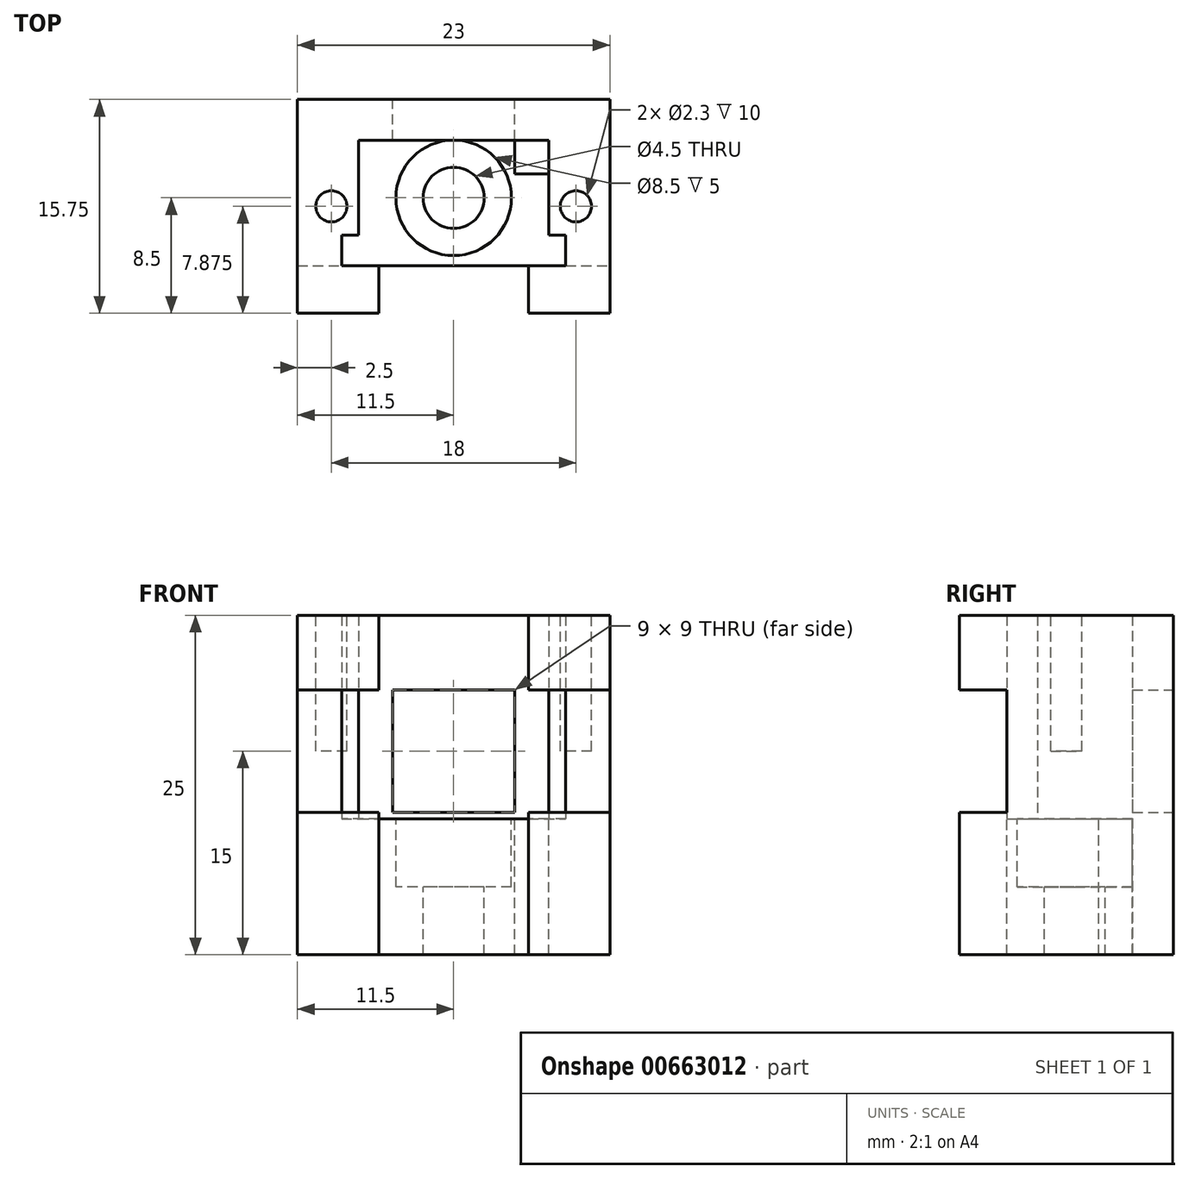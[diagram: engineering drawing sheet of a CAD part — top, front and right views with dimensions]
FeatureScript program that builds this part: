
annotation { "Feature Type Name" : "Feature", "Feature Type Description" : "" }
export const myFeature = defineFeature(function(context is Context, id is Id, definition is map)
    precondition{}
    {
        {
            var Q0;
            Q0=qCreatedBy(makeId("Top.planeOp"),FACE);
            var sketch = newSketch(context, id + "F0", { "sketchPlane" : qUnion([Q0])});
            skLineSegment(sketch, "E0.bottom", {"start": v(11.5, -10) * mm, "end": v(-11.5, -10) * mm});
            skLineSegment(sketch, "E0.top", {"start": v(11.5, 10) * mm, "end": v(-11.5, 10) * mm});
            skLineSegment(sketch, "E0.left", {"start": v(11.5, -10) * mm, "end": v(11.5, 10) * mm});
            skLineSegment(sketch, "E0.right", {"start": v(-11.5, -10) * mm, "end": v(-11.5, 10) * mm});
            skPoint(sketch, "E0.middle", {"position": v(0, 0) * mm});
            skSolve(sketch);
        }
        {
            var Q0;
            Q0=makeQuery(id+"F0.imprint","IMPRINT",FACE,{"disambiguationData":[TD([[makeQuery(id+"F0.imprint","IMPRINT",EDGE,{"derivedFrom":sQuery(id+"F0.wireOp",EDGE,"E0.bottom")}),-1.0]])]});
            extrude(context, id + "F1", {"entities" : qUnion([Q0]), "depth" : 10 * mm, "offsetDistance" : 25 * mm});
        }
        {
            var Q0;
            Q0=makeQuery(id+"F1.opExtrude","CAP_FACE",FACE,{"disambiguationData":[OSD([sQuery(id+"F0.wireOp",EDGE,"E0.bottom"),sQuery(id+"F0.wireOp",EDGE,"E0.top"),sQuery(id+"F0.wireOp",EDGE,"E0.left"),sQuery(id+"F0.wireOp",EDGE,"E0.right")])],"isStart":false});
            var sketch = newSketch(context, id + "F2", { "sketchPlane" : qUnion([Q0])});
            skLineSegment(sketch, "E1", {"start": v(-5.5, -10) * mm, "end": v(-5.5, -6.5) * mm});
            skLineSegment(sketch, "E2", {"start": v(-5.5, -6.5) * mm, "end": v(-8.25, -6.5) * mm});
            skLineSegment(sketch, "E3", {"start": v(-8.25, -6.5) * mm, "end": v(-8.25, -4.25) * mm});
            skLineSegment(sketch, "E4", {"start": v(-11.5, -0.75) * mm, "end": v(-11.5, -10) * mm});
            skLineSegment(sketch, "E5", {"start": v(-11.5, -10) * mm, "end": v(-5.5, -10) * mm});
            skLineSegment(sketch, "E6", {"start": v(5.5, -10) * mm, "end": v(5.5, -6.5) * mm});
            skLineSegment(sketch, "E7", {"start": v(5.5, -6.5) * mm, "end": v(8.25, -6.5) * mm});
            skLineSegment(sketch, "E8", {"start": v(8.25, -6.5) * mm, "end": v(8.25, -4.25) * mm});
            skLineSegment(sketch, "E9", {"start": v(11.5, -10) * mm, "end": v(5.5, -10) * mm});
            skLineSegment(sketch, "E10", {"start": v(-8.25, -4.25) * mm, "end": v(-7, -4.25) * mm});
            skLineSegment(sketch, "E11", {"start": v(-7, -4.25) * mm, "end": v(-7, -0.75) * mm});
            skLineSegment(sketch, "E12", {"start": v(-7, -0.75) * mm, "end": v(-11.5, -0.75) * mm});
            skLineSegment(sketch, "E13", {"start": v(8.25, -4.25) * mm, "end": v(7, -4.25) * mm});
            skLineSegment(sketch, "E14", {"start": v(7, -4.25) * mm, "end": v(7, -0.75) * mm});
            skLineSegment(sketch, "E15", {"start": v(7, -0.75) * mm, "end": v(11.5, -0.75) * mm});
            skLineSegment(sketch, "E16", {"start": v(11.5, -0.75) * mm, "end": v(11.5, -10) * mm});
            skSolve(sketch);
        }
        {
            var Q0;
            Q0=makeQuery(id+"F2.imprint","IMPRINT",FACE,{"disambiguationData":[TD([[makeQuery(id+"F2.imprint","IMPRINT",EDGE,{"derivedFrom":sQuery(id+"F2.wireOp",EDGE,"E6")}),-1.0]])]});
            var Q1;
            Q1=makeQuery(id+"F2.imprint","IMPRINT",FACE,{"disambiguationData":[TD([[makeQuery(id+"F2.imprint","IMPRINT",EDGE,{"derivedFrom":sQuery(id+"F2.wireOp",EDGE,"E1")}),1.0]])]});
            extrude(context, id + "F3", {"entities" : qUnion([Q0, Q1]), "operationType" : NewBodyOperationType.ADD, "depth" : 15 * mm, "offsetDistance" : 25 * mm});
        }
        {
            var Q0;
            Q0=makeQuery(id+"F1.opExtrude","CAP_FACE",FACE,{"disambiguationData":[OSD([sQuery(id+"F0.wireOp",EDGE,"E0.bottom"),sQuery(id+"F0.wireOp",EDGE,"E0.top"),sQuery(id+"F0.wireOp",EDGE,"E0.left"),sQuery(id+"F0.wireOp",EDGE,"E0.right")])],"isStart":false});
            var sketch = newSketch(context, id + "F4", { "sketchPlane" : qUnion([Q0])});
            skLineSegment(sketch, "E17.bottom", {"start": v(-5.5, -6.5) * mm, "end": v(5.5, -6.5) * mm});
            skLineSegment(sketch, "E17.top", {"start": v(-5.5, -10) * mm, "end": v(5.5, -10) * mm});
            skLineSegment(sketch, "E17.left", {"start": v(-5.5, -6.5) * mm, "end": v(-5.5, -10) * mm});
            skLineSegment(sketch, "E17.right", {"start": v(5.5, -6.5) * mm, "end": v(5.5, -10) * mm});
            skSolve(sketch);
        }
        {
            var Q0;
            Q0=makeQuery(id+"F4.imprint","IMPRINT",FACE,{"disambiguationData":[TD([[makeQuery(id+"F4.imprint","IMPRINT",EDGE,{"derivedFrom":sQuery(id+"F4.wireOp",EDGE,"E17.bottom")}),-1.0]])]});
            extrude(context, id + "F5", {"entities" : qUnion([Q0]), "operationType" : NewBodyOperationType.REMOVE, "endBound" : BoundingType.THROUGH_ALL, "oppositeDirection" : true, "depth" : 25 * mm, "offsetDistance" : 25 * mm});
        }
        {
            var Q0;
            Q0=makeQuery(id+"F3.opExtrude","SWEPT_FACE",FACE,{"disambiguationData":[OSD([sQuery(id+"F2.wireOp",EDGE,"E15")])]});
            var Q1;
            Q1=makeQuery(id+"F3.opExtrude","SWEPT_FACE",FACE,{"disambiguationData":[OSD([sQuery(id+"F2.wireOp",EDGE,"E12")])]});
            extrude(context, id + "F6", {"entities" : qUnion([Q0, Q1]), "operationType" : NewBodyOperationType.ADD, "depth" : 3.5 * mm, "offsetDistance" : 25 * mm});
        }
        {
            var Q0;
            Q0=makeQuery(id+"F6.opExtrude","CAP_FACE",FACE,{"disambiguationData":[OSD([sQuery(id+"F2.wireOp",EDGE,"E15")])],"isStart":false});
            var sketch = newSketch(context, id + "F7", { "sketchPlane" : qUnion([Q0])});
            skLineSegment(sketch, "E18.bottom", {"start": v(-11.5, 25) * mm, "end": v(11.5, 25) * mm});
            skLineSegment(sketch, "E18.top", {"start": v(-11.5, 10) * mm, "end": v(11.5, 10) * mm});
            skLineSegment(sketch, "E18.left", {"start": v(-11.5, 25) * mm, "end": v(-11.5, 10) * mm});
            skLineSegment(sketch, "E18.right", {"start": v(11.5, 25) * mm, "end": v(11.5, 10) * mm});
            skSolve(sketch);
        }
        {
            var Q0;
            {var subQ14=sQuery(id+"F7.wireOp",EDGE,"E18.left");Q0=makeQuery(id+"F7.imprint","IMPRINT",FACE,{"disambiguationData":[TD([[makeQuery(id+"F7.imprint","IMPRINT",EDGE,{"derivedFrom":subQ14}),1.0]])]});}
            var Q1;
            {var subQ0=sQuery(id+"F7.wireOp",EDGE,"E18.right");Q1=makeQuery(id+"F7.imprint","IMPRINT",FACE,{"disambiguationData":[TD([[makeQuery(id+"F7.imprint","IMPRINT",EDGE,{"derivedFrom":subQ0}),-1.0]])]});}
            var Q2;
            {var subQ1=sQuery(id+"F2.wireOp",EDGE,"E15");Q2=makeQuery(id+"F7.imprint","IMPRINT",FACE,{"disambiguationData":[TD([[makeQuery(id+"F7.imprint","IMPRINT",EDGE,{"derivedFrom":makeQuery(id+"F6.opExtrude","CAP_EDGE",EDGE,{"disambiguationData":[OSD([subQ1,sQuery(id+"FgVDrUZru3OC2iL_1.wireOp",EDGE,"WYO9HxfS-uRYI-8hlX-gOUZ-VxZhSrOw4LOQ.bottom")])],"isStart":false})}),-1.0]])]});}
            extrude(context, id + "F8", {"entities" : qUnion([Q0, Q1, Q2]), "operationType" : NewBodyOperationType.ADD, "depth" : 3 * mm, "offsetDistance" : 25 * mm});
        }
        {
            var Q0;
            Q0=makeQuery(id+"F1.opExtrude","SWEPT_FACE",FACE,{"disambiguationData":[OSD([sQuery(id+"F0.wireOp",EDGE,"E0.top")])]});
            extrude(context, id + "F9", {"entities" : qUnion([Q0]), "operationType" : NewBodyOperationType.ADD, "depth" : 7 * mm, "offsetDistance" : 25 * mm});
        }
        {
            var Q0;
            {var subQ0=sQuery(id+"F0.wireOp",EDGE,"E0.top");var subQ1=sQuery(id+"F0.wireOp",EDGE,"E0.right");var subQ4=sQuery(id+"F0.wireOp",EDGE,"E0.left");Q0=makeQuery(id+"F9.boolean.opBoolean","MERGE",FACE,{"derivedFrom":[makeQuery(id+"F8.boolean.opBoolean","SPLIT",FACE,{"disambiguationData":[TD([makeQuery(id+"F1.opExtrude","SWEPT_FACE",FACE,{"disambiguationData":[OSD([subQ0])]})])],"derivedFrom":makeQuery(id+"F00eLFHubhNlvBN_1.boolean.opBoolean","MERGE",FACE,{"derivedFrom":[makeQuery(id+"F1.opExtrude","CAP_FACE",FACE,{"disambiguationData":[OSD([sQuery(id+"F0.wireOp",EDGE,"E0.bottom"),subQ0,subQ4,subQ1])],"isStart":false})],"fromTools":[makeQuery(id+"F00eLFHubhNlvBN_1.opExtrude","SWEPT_FACE",FACE,{"disambiguationData":[OSD([sQuery(id+"FP4EQcqf4ovbBqS_1.wireOp",EDGE,"o0LPASs0-g3RE-xfQt-ammR-mRPTQmorZibc.bottom")])]})]})}),makeQuery(id+"F9.opExtrude","SWEPT_FACE",FACE,{"disambiguationData":[OSD([subQ0]),TDD([makeQuery(id+"F1.opExtrude","CAP_EDGE",EDGE,{"disambiguationData":[OSD([subQ0])],"isStart":false})])]})]});}
            var sketch = newSketch(context, id + "F10", { "sketchPlane" : qUnion([Q0])});
            skCircle(sketch, "E19", {"center": v(0, 11.25) * mm, "radius": 2.5 * mm});
            skCircle(sketch, "E20", {"center": v(0, 11.25) * mm, "radius": 5 * mm});
            skSolve(sketch);
        }
        {
            var Q0;
            Q0=makeQuery(id+"F10.imprint","IMPRINT",FACE,{"disambiguationData":[TD([[makeQuery(id+"F10.imprint","IMPRINT",EDGE,{"derivedFrom":sQuery(id+"F10.wireOp",EDGE,"E19")}),1.0]])]});
            extrude(context, id + "F11", {"entities" : qUnion([Q0]), "operationType" : NewBodyOperationType.REMOVE, "endBound" : BoundingType.THROUGH_ALL, "oppositeDirection" : true, "depth" : 25 * mm, "offsetDistance" : 25 * mm});
        }
        {
            var Q0;
            Q0=makeQuery(id+"F10.imprint","IMPRINT",FACE,{"disambiguationData":[TD([[makeQuery(id+"F10.imprint","IMPRINT",EDGE,{"derivedFrom":sQuery(id+"F10.wireOp",EDGE,"E19")}),-1.0]])]});
            extrude(context, id + "F12", {"entities" : qUnion([Q0]), "operationType" : NewBodyOperationType.REMOVE, "oppositeDirection" : true, "depth" : 4.5 * mm, "offsetDistance" : 25 * mm});
        }
        {
            var Q0;
            {var subQ0=sQuery(id+"F0.wireOp",EDGE,"E0.right");var subQ1=sQuery(id+"F2.wireOp",EDGE,"E4");Q0=makeQuery(id+"F9.boolean.opBoolean","MERGE",FACE,{"derivedFrom":[makeQuery(id+"F8.boolean.opBoolean","MERGE",FACE,{"derivedFrom":[makeQuery(id+"F6.boolean.opBoolean","MERGE",FACE,{"derivedFrom":[makeQuery(id+"F3.boolean.opBoolean","MERGE",FACE,{"derivedFrom":[makeQuery(id+"F1.opExtrude","SWEPT_FACE",FACE,{"disambiguationData":[OSD([subQ0])]}),makeQuery(id+"F3.opExtrude","SWEPT_FACE",FACE,{"disambiguationData":[OSD([subQ1])]})]}),makeQuery(id+"F6.opExtrude","SWEPT_FACE",FACE,{"disambiguationData":[OSD([subQ0,subQ1,sQuery(id+"F2.wireOp",EDGE,"E12")])]})]}),makeQuery(id+"F8.opExtrude","SWEPT_FACE",FACE,{"disambiguationData":[OSD([sQuery(id+"F7.wireOp",EDGE,"E18.right")])]})]}),makeQuery(id+"F9.opExtrude","SWEPT_FACE",FACE,{"disambiguationData":[OSD([sQuery(id+"F0.wireOp",EDGE,"E0.top"),subQ0])]})]});}
            var sketch = newSketch(context, id + "F13", { "sketchPlane" : qUnion([Q0])});
            skCircle(sketch, "E21", {"center": v(0, 5) * mm, "radius": 1.5 * mm});
            skSolve(sketch);
        }
        {
            var Q0;
            Q0=makeQuery(id+"F9.opExtrude","CAP_FACE",FACE,{"disambiguationData":[OSD([sQuery(id+"F0.wireOp",EDGE,"E0.top")])],"isStart":false});
            var sketch = newSketch(context, id + "F14", { "sketchPlane" : qUnion([Q0])});
            skCircle(sketch, "E22", {"center": v(8.5, 5) * mm, "radius": 1.5 * mm});
            skSolve(sketch);
        }
        {
            var Q0;
            Q0=makeQuery(id+"F8.boolean.opBoolean","SPLIT",FACE,{"disambiguationData":[TD([makeQuery(id+"F3.opExtrude","SWEPT_FACE",FACE,{"disambiguationData":[OSD([sQuery(id+"F2.wireOp",EDGE,"E1")])]})])],"derivedFrom":makeQuery(id+"F1.opExtrude","CAP_FACE",FACE,{"disambiguationData":[OSD([sQuery(id+"F0.wireOp",EDGE,"E0.bottom"),sQuery(id+"F0.wireOp",EDGE,"E0.top"),sQuery(id+"F0.wireOp",EDGE,"E0.left"),sQuery(id+"F0.wireOp",EDGE,"E0.right")])],"isStart":false})});
            var sketch = newSketch(context, id + "F15", { "sketchPlane" : qUnion([Q0])});
            skCircle(sketch, "E23", {"center": v(-4, 0) * mm, "radius": 1.5 * mm});
            skSolve(sketch);
        }
        {
            var Q0;
            {var subQ0=sQuery(id+"F2.wireOp",EDGE,"E15");var subQ1=sQuery(id+"F2.wireOp",EDGE,"E12");Q0=makeQuery(id+"F8.boolean.opBoolean","MERGE",FACE,{"derivedFrom":[makeQuery(id+"F6.boolean.opBoolean","MERGE",FACE,{"derivedFrom":[makeQuery(id+"F3.opExtrude","CAP_FACE",FACE,{"disambiguationData":[OSD([sQuery(id+"F2.wireOp",EDGE,"E1"),sQuery(id+"F2.wireOp",EDGE,"E2"),sQuery(id+"F2.wireOp",EDGE,"E3"),sQuery(id+"F2.wireOp",EDGE,"E4"),sQuery(id+"F2.wireOp",EDGE,"E5"),sQuery(id+"F2.wireOp",EDGE,"E10"),sQuery(id+"F2.wireOp",EDGE,"E11"),subQ1])],"isStart":false}),makeQuery(id+"F6.opExtrude","SWEPT_FACE",FACE,{"disambiguationData":[OSD([subQ1]),TDD([makeQuery(id+"F3.opExtrude","CAP_EDGE",EDGE,{"disambiguationData":[OSD([subQ1])],"isStart":false})])]})]}),makeQuery(id+"F6.boolean.opBoolean","MERGE",FACE,{"derivedFrom":[makeQuery(id+"F3.opExtrude","CAP_FACE",FACE,{"disambiguationData":[OSD([sQuery(id+"F2.wireOp",EDGE,"E6"),sQuery(id+"F2.wireOp",EDGE,"E7"),sQuery(id+"F2.wireOp",EDGE,"E8"),sQuery(id+"F2.wireOp",EDGE,"E9"),sQuery(id+"F2.wireOp",EDGE,"E13"),sQuery(id+"F2.wireOp",EDGE,"E14"),subQ0,sQuery(id+"F2.wireOp",EDGE,"E16")])],"isStart":false}),makeQuery(id+"F6.opExtrude","SWEPT_FACE",FACE,{"disambiguationData":[OSD([subQ0]),TDD([makeQuery(id+"F3.opExtrude","CAP_EDGE",EDGE,{"disambiguationData":[OSD([subQ0])],"isStart":false})])]})]}),makeQuery(id+"F8.opExtrude","SWEPT_FACE",FACE,{"disambiguationData":[OSD([sQuery(id+"F7.wireOp",EDGE,"E18.bottom")])]})]});}
            var sketch = newSketch(context, id + "F16", { "sketchPlane" : qUnion([Q0])});
            skCircle(sketch, "E24", {"center": v(-9, -2.13) * mm, "radius": 1.15 * mm});
            skCircle(sketch, "E25", {"center": v(9, -2.13) * mm, "radius": 1.15 * mm});
            skSolve(sketch);
        }
        {
            var Q0;
            Q0=makeQuery(id+"F16.imprint","IMPRINT",FACE,{"disambiguationData":[TD([[makeQuery(id+"F16.imprint","IMPRINT",EDGE,{"derivedFrom":sQuery(id+"F16.wireOp",EDGE,"E24")}),1.0]])]});
            var Q1;
            Q1=makeQuery(id+"F16.imprint","IMPRINT",FACE,{"disambiguationData":[TD([[makeQuery(id+"F16.imprint","IMPRINT",EDGE,{"derivedFrom":sQuery(id+"F16.wireOp",EDGE,"E25")}),1.0]])]});
            extrude(context, id + "F17", {"entities" : qUnion([Q0, Q1]), "operationType" : NewBodyOperationType.REMOVE, "oppositeDirection" : true, "depth" : 10 * mm, "offsetDistance" : 25 * mm});
        }
        {
            var Q0;
            Q0=makeQuery(id+"F8.boolean.opBoolean","SPLIT",FACE,{"disambiguationData":[TD([makeQuery(id+"F3.opExtrude","SWEPT_FACE",FACE,{"disambiguationData":[OSD([sQuery(id+"F2.wireOp",EDGE,"E1")])]})])],"derivedFrom":makeQuery(id+"F1.opExtrude","CAP_FACE",FACE,{"disambiguationData":[OSD([sQuery(id+"F0.wireOp",EDGE,"E0.bottom"),sQuery(id+"F0.wireOp",EDGE,"E0.top"),sQuery(id+"F0.wireOp",EDGE,"E0.left"),sQuery(id+"F0.wireOp",EDGE,"E0.right")])],"isStart":false})});
            var sketch = newSketch(context, id + "F18", { "sketchPlane" : qUnion([Q0])});
            skPoint(sketch, "E26", {"position": v(0, -1.5) * mm});
            skLineSegment(sketch, "E27", {"start": v(0, -1.5) * mm, "end": v(0, -6.5) * mm, "construction": true});
            skLineSegment(sketch, "E28", {"start": v(0, -1.5) * mm, "end": v(0, 2.75) * mm, "construction": true});
            skCircle(sketch, "E29", {"center": v(0, -1.5) * mm, "radius": 2.25 * mm});
            skCircle(sketch, "E30", {"center": v(0, -1.5) * mm, "radius": 4.25 * mm});
            skSolve(sketch);
        }
        {
            var Q0;
            Q0=makeQuery(id+"F18.imprint","IMPRINT",FACE,{"disambiguationData":[TD([[makeQuery(id+"F18.imprint","IMPRINT",EDGE,{"derivedFrom":sQuery(id+"F18.wireOp",EDGE,"E29")}),1.0]])]});
            extrude(context, id + "F19", {"entities" : qUnion([Q0]), "operationType" : NewBodyOperationType.REMOVE, "endBound" : BoundingType.THROUGH_ALL, "oppositeDirection" : true, "depth" : 25 * mm, "offsetDistance" : 25 * mm});
        }
        {
            var Q0;
            Q0=makeQuery(id+"F18.imprint","IMPRINT",FACE,{"disambiguationData":[TD([[makeQuery(id+"F18.imprint","IMPRINT",EDGE,{"derivedFrom":sQuery(id+"F18.wireOp",EDGE,"E29")}),-1.0]])]});
            extrude(context, id + "F20", {"entities" : qUnion([Q0]), "operationType" : NewBodyOperationType.REMOVE, "oppositeDirection" : true, "depth" : 5 * mm, "offsetDistance" : 25 * mm});
        }
        {
            var Q0;
            {var subQ0=sQuery(id+"F0.wireOp",EDGE,"E0.top");var subQ1=sQuery(id+"F0.wireOp",EDGE,"E0.right");var subQ2=sQuery(id+"F0.wireOp",EDGE,"E0.left");Q0=makeQuery(id+"F9.boolean.opBoolean","MERGE",FACE,{"derivedFrom":[makeQuery(id+"F8.boolean.opBoolean","SPLIT",FACE,{"disambiguationData":[TD([makeQuery(id+"F1.opExtrude","SWEPT_FACE",FACE,{"disambiguationData":[OSD([subQ0])]})])],"derivedFrom":makeQuery(id+"F1.opExtrude","CAP_FACE",FACE,{"disambiguationData":[OSD([sQuery(id+"F0.wireOp",EDGE,"E0.bottom"),subQ0,subQ2,subQ1])],"isStart":false})}),makeQuery(id+"F9.opExtrude","SWEPT_FACE",FACE,{"disambiguationData":[OSD([subQ0]),TDD([makeQuery(id+"F1.opExtrude","CAP_EDGE",EDGE,{"disambiguationData":[OSD([subQ0])],"isStart":false})])]})]});}
            var Q1;
            Q1=makeQuery(id+"F12.boolean.opBoolean","COPY",FACE,{"derivedFrom":makeQuery(id+"F12.opExtrude","CAP_FACE",FACE,{"disambiguationData":[OSD([sQuery(id+"F10.wireOp",EDGE,"E19"),sQuery(id+"F10.wireOp",EDGE,"E20")])],"isStart":false})});
            extrude(context, id + "F21", {"entities" : qUnion([Q0, Q1]), "operationType" : NewBodyOperationType.REMOVE, "endBound" : BoundingType.THROUGH_ALL, "oppositeDirection" : true, "depth" : 25 * mm, "offsetDistance" : 25 * mm});
        }
        {
            var Q0;
            Q0=makeQuery(id+"F8.boolean.opBoolean","SPLIT",FACE,{"disambiguationData":[TD([makeQuery(id+"F3.opExtrude","SWEPT_FACE",FACE,{"disambiguationData":[OSD([sQuery(id+"F2.wireOp",EDGE,"E1")])]})])],"derivedFrom":makeQuery(id+"F1.opExtrude","CAP_FACE",FACE,{"disambiguationData":[OSD([sQuery(id+"F0.wireOp",EDGE,"E0.bottom"),sQuery(id+"F0.wireOp",EDGE,"E0.top"),sQuery(id+"F0.wireOp",EDGE,"E0.left"),sQuery(id+"F0.wireOp",EDGE,"E0.right")])],"isStart":false})});
            var sketch = newSketch(context, id + "F22", { "sketchPlane" : qUnion([Q0])});
            skLineSegment(sketch, "E31.bottom", {"start": v(-7, 2.75) * mm, "end": v(-5, 2.75) * mm});
            skLineSegment(sketch, "E31.top", {"start": v(-7, 0.75) * mm, "end": v(-5, 0.75) * mm});
            skLineSegment(sketch, "E31.left", {"start": v(-7, 2.75) * mm, "end": v(-7, 0.75) * mm});
            skLineSegment(sketch, "E31.right", {"start": v(-5, 2.75) * mm, "end": v(-5, 0.75) * mm});
            skLineSegment(sketch, "E32.bottom", {"start": v(7, 2.75) * mm, "end": v(4.5, 2.75) * mm});
            skLineSegment(sketch, "E32.top", {"start": v(7, 0.25) * mm, "end": v(4.5, 0.25) * mm});
            skLineSegment(sketch, "E32.left", {"start": v(7, 2.75) * mm, "end": v(7, 0.25) * mm});
            skLineSegment(sketch, "E32.right", {"start": v(4.5, 2.75) * mm, "end": v(4.5, 0.25) * mm});
            skSolve(sketch);
        }
        {
            var Q0;
            Q0=makeQuery(id+"F22.imprint","IMPRINT",FACE,{"disambiguationData":[TD([[makeQuery(id+"F22.imprint","IMPRINT",EDGE,{"derivedFrom":sQuery(id+"F22.wireOp",EDGE,"E32.bottom")}),-1.0]])]});
            extrude(context, id + "F23", {"entities" : qUnion([Q0]), "operationType" : NewBodyOperationType.REMOVE, "endBound" : BoundingType.THROUGH_ALL, "oppositeDirection" : true, "depth" : 25 * mm, "offsetDistance" : 25 * mm});
        }
        {
            var Q0;
            {var subQ0=sQuery(id+"F7.wireOp",EDGE,"E18.top");Q0=makeQuery(id+"F21.boolean.opBoolean","MERGE",FACE,{"derivedFrom":[makeQuery(id+"F8.opExtrude","CAP_FACE",FACE,{"disambiguationData":[OSD([sQuery(id+"F7.wireOp",EDGE,"E18.bottom"),subQ0,sQuery(id+"F7.wireOp",EDGE,"E18.left"),sQuery(id+"F7.wireOp",EDGE,"E18.right")])],"isStart":false})],"fromTools":[makeQuery(id+"F21.opExtrude","SWEPT_FACE",FACE,{"disambiguationData":[OSD([subQ0])]})]});}
            var sketch = newSketch(context, id + "F24", { "sketchPlane" : qUnion([Q0])});
            skLineSegment(sketch, "E33.bottom", {"start": v(-4.5, 19.5) * mm, "end": v(4.5, 19.5) * mm});
            skLineSegment(sketch, "E33.top", {"start": v(-4.5, 10.5) * mm, "end": v(4.5, 10.5) * mm});
            skLineSegment(sketch, "E33.left", {"start": v(-4.5, 19.5) * mm, "end": v(-4.5, 10.5) * mm});
            skLineSegment(sketch, "E33.right", {"start": v(4.5, 19.5) * mm, "end": v(4.5, 10.5) * mm});
            skSolve(sketch);
        }
        {
            var Q0;
            Q0=makeQuery(id+"F24.imprint","IMPRINT",FACE,{"disambiguationData":[TD([[makeQuery(id+"F24.imprint","IMPRINT",EDGE,{"derivedFrom":sQuery(id+"F24.wireOp",EDGE,"E33.bottom")}),-1.0]])]});
            extrude(context, id + "F25", {"entities" : qUnion([Q0]), "operationType" : NewBodyOperationType.REMOVE, "endBound" : BoundingType.THROUGH_ALL, "oppositeDirection" : true, "depth" : 25 * mm, "offsetDistance" : 25 * mm});
        }
        {
            var Q0;
            {var subQ0=sQuery(id+"F0.wireOp",EDGE,"E0.left");var subQ1=sQuery(id+"F2.wireOp",EDGE,"E16");Q0=makeQuery(id+"F9.boolean.opBoolean","MERGE",FACE,{"derivedFrom":[makeQuery(id+"F8.boolean.opBoolean","MERGE",FACE,{"derivedFrom":[makeQuery(id+"F6.boolean.opBoolean","MERGE",FACE,{"derivedFrom":[makeQuery(id+"F3.boolean.opBoolean","MERGE",FACE,{"derivedFrom":[makeQuery(id+"F1.opExtrude","SWEPT_FACE",FACE,{"disambiguationData":[OSD([subQ0])]}),makeQuery(id+"F3.opExtrude","SWEPT_FACE",FACE,{"disambiguationData":[OSD([subQ1])]})]}),makeQuery(id+"F6.opExtrude","SWEPT_FACE",FACE,{"disambiguationData":[OSD([subQ0,sQuery(id+"F2.wireOp",EDGE,"E15"),subQ1])]})]}),makeQuery(id+"F8.opExtrude","SWEPT_FACE",FACE,{"disambiguationData":[OSD([sQuery(id+"F7.wireOp",EDGE,"E18.left")])]})]}),makeQuery(id+"F9.opExtrude","SWEPT_FACE",FACE,{"disambiguationData":[OSD([sQuery(id+"F0.wireOp",EDGE,"E0.top"),subQ0])]})]});}
            var sketch = newSketch(context, id + "F26", { "sketchPlane" : qUnion([Q0])});
            skLineSegment(sketch, "E34.bottom", {"start": v(-10, 10.5) * mm, "end": v(-6.5, 10.5) * mm});
            skLineSegment(sketch, "E34.top", {"start": v(-10, 19.5) * mm, "end": v(-6.5, 19.5) * mm});
            skLineSegment(sketch, "E34.left", {"start": v(-10, 10.5) * mm, "end": v(-10, 19.5) * mm});
            skLineSegment(sketch, "E34.right", {"start": v(-6.5, 10.5) * mm, "end": v(-6.5, 19.5) * mm});
            skSolve(sketch);
        }
        {
            var Q0;
            Q0=makeQuery(id+"F26.imprint","IMPRINT",FACE,{"disambiguationData":[TD([[makeQuery(id+"F26.imprint","IMPRINT",EDGE,{"derivedFrom":sQuery(id+"F26.wireOp",EDGE,"E34.bottom")}),1.0]])]});
            extrude(context, id + "F27", {"entities" : qUnion([Q0]), "operationType" : NewBodyOperationType.REMOVE, "endBound" : BoundingType.THROUGH_ALL, "oppositeDirection" : true, "depth" : 25 * mm, "offsetDistance" : 25 * mm});
        }
    });
